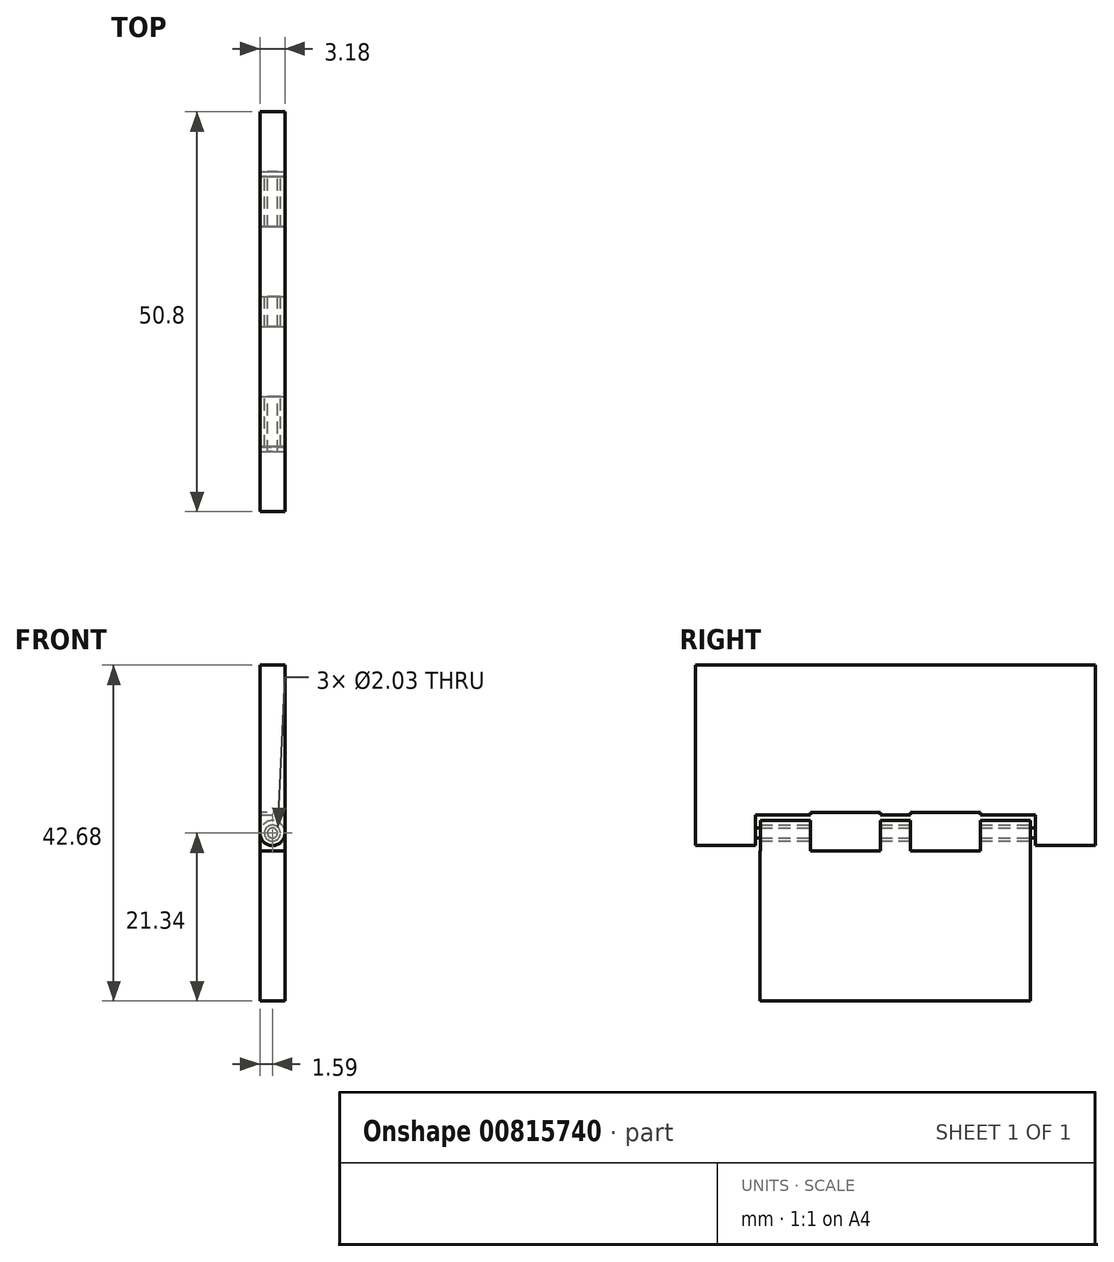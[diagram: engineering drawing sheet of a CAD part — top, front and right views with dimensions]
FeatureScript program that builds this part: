
annotation { "Feature Type Name" : "Feature", "Feature Type Description" : "" }
export const myFeature = defineFeature(function(context is Context, id is Id, definition is map)
    precondition{}
    {
        {
            var Q0;
            Q0=qCreatedBy(makeId("Front.planeOp"),FACE);
            var sketch = newSketch(context, id + "F0", { "sketchPlane" : qUnion([Q0])});
            skCircle(sketch, "E0", {"center": v(0, 0) * mm, "radius": 0.64 * mm});
            skSolve(sketch);
        }
        {
            var Q0;
            Q0 = qSketchRegion(id + "F0", true);
            extrude(context, id + "F1", {"entities" : qUnion([Q0]), "depth" : 50.8 * mm, "offsetDistance" : 25.4 * mm});
        }
        {
            var Q0;
            Q0=qCreatedBy(makeId("Front.planeOp"),FACE);
            var sketch = newSketch(context, id + "F2", { "sketchPlane" : qUnion([Q0])});
            skCircle(sketch, "E1", {"center": v(0, 0) * mm, "radius": 1.59 * mm});
            skSolve(sketch);
        }
        {
            var Q0;
            Q0=makeQuery(id+"F2.imprint","IMPRINT",FACE,{"disambiguationData":[TD([[makeQuery(id+"F2.imprint","IMPRINT",EDGE,{"derivedFrom":sQuery(id+"F2.wireOp",EDGE,"E1")}),1.0]])]});
            extrude(context, id + "F3", {"entities" : qUnion([Q0]), "operationType" : NewBodyOperationType.ADD, "depth" : 7.62 * mm, "offsetDistance" : 25.4 * mm});
        }
        {
            var Q0;
            Q0=makeQuery(id+"F1.opExtrude","CAP_FACE",FACE,{"disambiguationData":[OSD([sQuery(id+"F0.wireOp",EDGE,"E0")])],"isStart":false});
            var sketch = newSketch(context, id + "F4", { "sketchPlane" : qUnion([Q0])});
            skCircle(sketch, "E2", {"center": v(0, 0) * mm, "radius": 1.59 * mm});
            skSolve(sketch);
        }
        {
            var Q0;
            Q0 = qSketchRegion(id + "F4", true);
            extrude(context, id + "F5", {"entities" : qUnion([Q0]), "operationType" : NewBodyOperationType.ADD, "oppositeDirection" : true, "depth" : 7.62 * mm, "offsetDistance" : 25.4 * mm});
        }
        {
            var Q0;
            Q0=makeQuery(id+"F3.opExtrude","CAP_FACE",FACE,{"disambiguationData":[OSD([sQuery(id+"F2.wireOp",EDGE,"E1")])],"isStart":false});
            cPlane(context, id + "F6", {"entities" : qUnion([Q0]), "cplaneType" : CPlaneType.OFFSET, "offset" : 7.62 * mm, "width" : 152.4 * mm, "height" : 152.4 * mm});
        }
        {
            var Q0;
            Q0=qCreatedBy(id+"F6.planeOp",FACE);
            var sketch = newSketch(context, id + "F7", { "sketchPlane" : qUnion([Q0])});
            skCircle(sketch, "E3", {"center": v(0, 0) * mm, "radius": 1.59 * mm});
            skSolve(sketch);
        }
        {
            var Q0;
            Q0 = qSketchRegion(id + "F7", true);
            extrude(context, id + "F8", {"entities" : qUnion([Q0]), "operationType" : NewBodyOperationType.ADD, "depth" : 7.62 * mm, "offsetDistance" : 25.4 * mm});
        }
        {
            var Q0;
            Q0=makeQuery(id+"F5.opExtrude","CAP_FACE",FACE,{"disambiguationData":[OSD([sQuery(id+"F4.wireOp",EDGE,"E2")])],"isStart":false});
            cPlane(context, id + "F9", {"entities" : qUnion([Q0]), "cplaneType" : CPlaneType.OFFSET, "offset" : 7.62 * mm, "width" : 152.4 * mm, "height" : 152.4 * mm});
        }
        {
            var Q0;
            Q0=qCreatedBy(id+"F9.planeOp",FACE);
            var sketch = newSketch(context, id + "F10", { "sketchPlane" : qUnion([Q0])});
            skCircle(sketch, "E4", {"center": v(0, 0) * mm, "radius": 1.59 * mm});
            skSolve(sketch);
        }
        {
            var Q0;
            Q0 = qSketchRegion(id + "F10", true);
            extrude(context, id + "F11", {"entities" : qUnion([Q0]), "operationType" : NewBodyOperationType.ADD, "depth" : 7.62 * mm, "offsetDistance" : 25.4 * mm});
        }
        {
            var Q0;
            Q0=qCreatedBy(makeId("Top.planeOp"),FACE);
            cPlane(context, id + "F12", {"entities" : qUnion([Q0]), "cplaneType" : CPlaneType.OFFSET, "offset" : 2.3 * mm, "width" : 152.4 * mm, "height" : 152.4 * mm});
        }
        {
            var Q0;
            Q0=qCreatedBy(id+"F12.planeOp",FACE);
            var sketch = newSketch(context, id + "F13", { "sketchPlane" : qUnion([Q0])});
            skLineSegment(sketch, "E5", {"start": v(-1.59, -50.8) * mm, "end": v(-1.59, -43.18) * mm});
            skLineSegment(sketch, "E6", {"start": v(1.59, -43.18) * mm, "end": v(1.59, -50.8) * mm});
            skLineSegment(sketch, "E7", {"start": v(-1.59, -35.56) * mm, "end": v(-1.59, -27.94) * mm});
            skLineSegment(sketch, "E8", {"start": v(1.59, -27.94) * mm, "end": v(1.59, -35.56) * mm});
            skLineSegment(sketch, "E9", {"start": v(1.59, -15.24) * mm, "end": v(1.59, -22.86) * mm});
            skLineSegment(sketch, "E10", {"start": v(-1.59, -22.86) * mm, "end": v(-1.59, -15.24) * mm});
            skLineSegment(sketch, "E11", {"start": v(1.59, 0) * mm, "end": v(1.59, -7.62) * mm});
            skLineSegment(sketch, "E12", {"start": v(-1.59, -7.62) * mm, "end": v(-1.59, 0) * mm});
            skLineSegment(sketch, "E13", {"start": v(-1.59, -50.8) * mm, "end": v(1.59, -50.8) * mm});
            skLineSegment(sketch, "E14", {"start": v(-1.59, -43.18) * mm, "end": v(1.59, -43.18) * mm});
            skLineSegment(sketch, "E15", {"start": v(-1.59, -35.56) * mm, "end": v(1.59, -35.56) * mm});
            skLineSegment(sketch, "E16", {"start": v(-1.59, -27.94) * mm, "end": v(1.59, -27.94) * mm});
            skLineSegment(sketch, "E17", {"start": v(-1.59, -22.86) * mm, "end": v(1.59, -22.86) * mm});
            skLineSegment(sketch, "E18", {"start": v(-1.59, -15.24) * mm, "end": v(1.59, -15.24) * mm});
            skLineSegment(sketch, "E19", {"start": v(-1.59, -7.62) * mm, "end": v(1.59, -7.62) * mm});
            skLineSegment(sketch, "E20", {"start": v(-1.59, 0) * mm, "end": v(1.59, 0) * mm});
            skSolve(sketch);
        }
        {
            var Q0;
            Q0 = qSketchRegion(id + "F13", true);
            var Q1;
            Q1=makeQuery(id+"F5.opExtrude","SWEPT_FACE",FACE,{"disambiguationData":[OSD([sQuery(id+"F4.wireOp",EDGE,"E2")])]});
            extrude(context, id + "F14", {"entities" : qUnion([Q0]), "operationType" : NewBodyOperationType.ADD, "endBound" : BoundingType.UP_TO_SURFACE, "oppositeDirection" : true, "depth" : 25.4 * mm, "endBoundEntityFace" : qUnion([Q1]), "offsetDistance" : 25.4 * mm});
        }
        {
            var Q0;
            Q0=makeQuery(id+"F14.opExtrude","CAP_FACE",FACE,{"disambiguationData":[OSD([sQuery(id+"F13.wireOp",EDGE,"E5"),sQuery(id+"F13.wireOp",EDGE,"E6"),sQuery(id+"F13.wireOp",EDGE,"E13"),sQuery(id+"F13.wireOp",EDGE,"E14")])],"isStart":true});
            var sketch = newSketch(context, id + "F15", { "sketchPlane" : qUnion([Q0])});
            skLineSegment(sketch, "E21", {"start": v(-1.59, -50.8) * mm, "end": v(-1.59, 0) * mm});
            skLineSegment(sketch, "E22", {"start": v(-1.59, 0) * mm, "end": v(1.59, 0) * mm});
            skLineSegment(sketch, "E23", {"start": v(1.59, 0) * mm, "end": v(1.59, -50.8) * mm});
            skLineSegment(sketch, "E24", {"start": v(1.59, -50.8) * mm, "end": v(-1.59, -50.8) * mm});
            skSolve(sketch);
        }
        {
            var Q0;
            Q0 = qSketchRegion(id + "F15", true);
            extrude(context, id + "F16", {"entities" : qUnion([Q0]), "operationType" : NewBodyOperationType.ADD, "depth" : 19.05 * mm, "offsetDistance" : 25.4 * mm});
        }
        {
            var Q0;
            Q0=makeQuery(id+"F14.boolean.opBoolean","MERGE",FACE,{"derivedFrom":[makeQuery(id+"F3.opExtrude","CAP_FACE",FACE,{"disambiguationData":[OSD([sQuery(id+"F2.wireOp",EDGE,"E1")])],"isStart":false}),makeQuery(id+"F14.opExtrude","SWEPT_FACE",FACE,{"disambiguationData":[OSD([sQuery(id+"F13.wireOp",EDGE,"E19")])]})]});
            cPlane(context, id + "F17", {"entities" : qUnion([Q0]), "cplaneType" : CPlaneType.OFFSET, "offset" : 0.64 * mm, "width" : 152.4 * mm, "height" : 152.4 * mm});
        }
        {
            var Q0;
            Q0=qCreatedBy(id+"F17.planeOp",FACE);
            var sketch = newSketch(context, id + "F18", { "sketchPlane" : qUnion([Q0])});
            skCircle(sketch, "E25", {"center": v(0, 0) * mm, "radius": 1.59 * mm});
            skCircle(sketch, "E26", {"center": v(0, 0) * mm, "radius": 1.02 * mm});
            skSolve(sketch);
        }
        {
            var Q0;
            Q0 = qSketchRegion(id + "F18", true);
            extrude(context, id + "F19", {"entities" : qUnion([Q0]), "depth" : 34.3 * mm, "offsetDistance" : 25.4 * mm});
        }
        {
            var Q0;
            Q0=qCreatedBy(makeId("Top.planeOp"),FACE);
            cPlane(context, id + "F20", {"entities" : qUnion([Q0]), "cplaneType" : CPlaneType.OFFSET, "offset" : 2.3 * mm, "oppositeDirection" : true, "width" : 152.4 * mm, "height" : 152.4 * mm});
        }
        {
            var Q0;
            Q0=qCreatedBy(id+"F20.planeOp",FACE);
            var sketch = newSketch(context, id + "F21", { "sketchPlane" : qUnion([Q0])});
            skLineSegment(sketch, "E27.0", {"start": v(-1.59, -14.6) * mm, "end": v(-1.59, -8.25) * mm});
            skLineSegment(sketch, "E28.0", {"start": v(1.59, -8.25) * mm, "end": v(1.59, -14.6) * mm});
            skLineSegment(sketch, "E29.0", {"start": v(1.59, -23.5) * mm, "end": v(1.59, -27.3) * mm});
            skLineSegment(sketch, "E30.0", {"start": v(1.59, -36.2) * mm, "end": v(1.59, -42.55) * mm});
            skLineSegment(sketch, "E31.0", {"start": v(-1.59, -42.55) * mm, "end": v(-1.59, -36.2) * mm});
            skLineSegment(sketch, "E32.0", {"start": v(-1.59, -27.3) * mm, "end": v(-1.59, -23.5) * mm});
            skLineSegment(sketch, "E33.0", {"start": v(-1.59, -8.25) * mm, "end": v(1.59, -8.25) * mm});
            skLineSegment(sketch, "E34.0", {"start": v(-1.59, -14.6) * mm, "end": v(1.59, -14.6) * mm});
            skLineSegment(sketch, "E35.0", {"start": v(-1.59, -23.5) * mm, "end": v(1.59, -23.5) * mm});
            skLineSegment(sketch, "E36.0", {"start": v(-1.59, -27.3) * mm, "end": v(1.59, -27.3) * mm});
            skLineSegment(sketch, "E37.0", {"start": v(-1.59, -36.2) * mm, "end": v(1.59, -36.2) * mm});
            skLineSegment(sketch, "E38.0", {"start": v(-1.59, -42.55) * mm, "end": v(1.59, -42.55) * mm});
            skPoint(sketch, "E39.orphan", {"position": v(-1.59, -43.18) * mm});
            skPoint(sketch, "E40.orphan", {"position": v(1.59, -43.18) * mm});
            skPoint(sketch, "E41.end.orphan", {"position": v(1.59, -35.56) * mm});
            skPoint(sketch, "E41.start.orphan", {"position": v(-1.59, -35.56) * mm});
            skPoint(sketch, "E42.orphan", {"position": v(1.59, -27.94) * mm});
            skPoint(sketch, "E43.orphan", {"position": v(-1.59, -27.94) * mm});
            skPoint(sketch, "E44.orphan", {"position": v(-1.59, -22.86) * mm});
            skPoint(sketch, "E45.orphan", {"position": v(1.59, -22.86) * mm});
            skPoint(sketch, "E46.orphan", {"position": v(-1.59, -7.62) * mm});
            skPoint(sketch, "E47.orphan", {"position": v(1.59, -7.62) * mm});
            skPoint(sketch, "E48.end.orphan", {"position": v(1.59, -15.24) * mm});
            skPoint(sketch, "E48.start.orphan", {"position": v(-1.59, -15.24) * mm});
            skSolve(sketch);
        }
        {
            var Q0;
            Q0 = qSketchRegion(id + "F21", true);
            var Q1;
            Q1=makeQuery(id+"F19.opExtrude","SWEPT_FACE",FACE,{"disambiguationData":[OSD([sQuery(id+"F18.wireOp",EDGE,"E25")])]});
            extrude(context, id + "F22", {"entities" : qUnion([Q0]), "operationType" : NewBodyOperationType.ADD, "endBound" : BoundingType.UP_TO_SURFACE, "depth" : 25.4 * mm, "endBoundEntityFace" : qUnion([Q1]), "offsetDistance" : 25.4 * mm});
        }
        {
            var Q0;
            Q0=makeQuery(id+"F22.opExtrude","CAP_FACE",FACE,{"disambiguationData":[OSD([sQuery(id+"F21.wireOp",EDGE,"E27.0"),sQuery(id+"F21.wireOp",EDGE,"E28.0"),sQuery(id+"F21.wireOp",EDGE,"E33.0"),sQuery(id+"F21.wireOp",EDGE,"E34.0")])],"isStart":true});
            var sketch = newSketch(context, id + "F23", { "sketchPlane" : qUnion([Q0])});
            skLineSegment(sketch, "E49", {"start": v(-1.59, 8.25) * mm, "end": v(-1.59, 42.63) * mm});
            skLineSegment(sketch, "E50", {"start": v(-1.59, 42.63) * mm, "end": v(1.59, 42.63) * mm});
            skLineSegment(sketch, "E51", {"start": v(1.59, 42.63) * mm, "end": v(1.59, 8.25) * mm});
            skLineSegment(sketch, "E52", {"start": v(1.59, 8.25) * mm, "end": v(-1.59, 8.25) * mm});
            skSolve(sketch);
        }
        {
            var Q0;
            Q0 = qSketchRegion(id + "F23", true);
            extrude(context, id + "F24", {"entities" : qUnion([Q0]), "operationType" : NewBodyOperationType.ADD, "depth" : 19.05 * mm, "offsetDistance" : 25.4 * mm});
        }
        {
            var Q0;
            Q0=makeQuery(id+"F24.boolean.opBoolean","MERGE",FACE,{"derivedFrom":[makeQuery(id+"F22.opExtrude","SWEPT_FACE",FACE,{"disambiguationData":[OSD([sQuery(id+"F21.wireOp",EDGE,"E27.0")])]}),makeQuery(id+"F22.opExtrude","SWEPT_FACE",FACE,{"disambiguationData":[OSD([sQuery(id+"F21.wireOp",EDGE,"E31.0")])]}),makeQuery(id+"F22.opExtrude","SWEPT_FACE",FACE,{"disambiguationData":[OSD([sQuery(id+"F21.wireOp",EDGE,"E32.0")])]}),makeQuery(id+"F24.opExtrude","SWEPT_FACE",FACE,{"disambiguationData":[OSD([sQuery(id+"F23.wireOp",EDGE,"E49")])]})]});
            var sketch = newSketch(context, id + "F25", { "sketchPlane" : qUnion([Q0])});
            skLineSegment(sketch, "E53", {"start": v(14.6, -2.29) * mm, "end": v(14.6, 2.6) * mm});
            skLineSegment(sketch, "E54", {"start": v(14.6, 2.6) * mm, "end": v(23.5, 2.6) * mm});
            skLineSegment(sketch, "E55", {"start": v(23.5, 2.6) * mm, "end": v(23.5, -2.29) * mm});
            skLineSegment(sketch, "E56", {"start": v(23.5, -2.29) * mm, "end": v(14.6, -2.29) * mm});
            skLineSegment(sketch, "E57", {"start": v(27.3, -2.29) * mm, "end": v(36.2, -2.29) * mm});
            skLineSegment(sketch, "E58", {"start": v(36.2, -2.29) * mm, "end": v(36.2, 2.6) * mm});
            skLineSegment(sketch, "E59", {"start": v(36.2, 2.6) * mm, "end": v(27.3, 2.6) * mm});
            skLineSegment(sketch, "E60", {"start": v(27.3, 2.6) * mm, "end": v(27.3, -2.29) * mm});
            skSolve(sketch);
        }
        {
            var Q0;
            Q0 = qSketchRegion(id + "F25", true);
            extrude(context, id + "F26", {"entities" : qUnion([Q0]), "operationType" : NewBodyOperationType.REMOVE, "oppositeDirection" : true, "depth" : 25.4 * mm, "offsetDistance" : 25.4 * mm});
        }
    });
